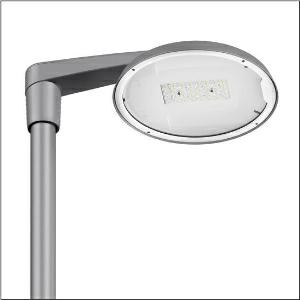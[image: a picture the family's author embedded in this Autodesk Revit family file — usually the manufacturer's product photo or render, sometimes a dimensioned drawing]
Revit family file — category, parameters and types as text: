
# Revit family: dl_r__50_iq_mini___st0_5a_5xa248b31f08fe_5b8c
name_source: partatom
category: Lighting Fixtures
units: mm (PartAtom-declared; Revit-internal decimal feet)

## family parameters
Cut with Voids When Loaded = No
Host = Face
Light Source = No
Part Type = Normal
Room Calculation Point = No
Round Connector Dimension = Use Diameter
Shared = No

## types (1)
- --- (1 x LED, 2700 lm, 16.3 W, 3000K)
    Apparent Load = 16 VA
    CIE Flux Codes = 41 75 97 100 100
    Color Rendering = 70
    Color Temperature = 3000K
    Default Elevation = 1800 mm
    Description = DL® 50 iQ mini, mast luminaire, primary light control with lens, of PMMA, primary optical cover: cover, of toughened safety glass, transparent, light distribution: ST0.5a, light emission: direct distribution, primary light characteristic: asymmetric, installation type: side-entry, post-top, LED, High Power LED, rated luminous flux: 2.700lm, luminous efficacy: 166lm/W, light colour: 730, colour temperature: 3000K, control: optimised constant luminous flux control (CLO 2.0), Desk-Remote (wireless, voltage-free reading and setting of iQ features in the workshop via application-optimized NFC function/RFID function), Light-Fading, Smart-Wire, Night-Set, Lumen-Switch, Temp-Guard, Auto-Match, Street-Remote, mains connection: 230..240V, AC, 50/60Hz, connection cable pre-assembled, cable length: 6,5m, start of lifetime: 16W, end of service life: 17W, reduction: 8W, luminaire housing, of diecast aluminium, powder-coated, Siteco® metallic grey (DB 702S), inclination adjustable: 0°, 5°, 10° (post-top) | 0°, -5°, -10°, -15° (side-entry), please order mast post-top element or mast side-entry element separately, diameter: 500mm, height: 115mm, post-top: for spigot size d x l = 76 x 100mm; with reducer (optional accessory) 60 x 100mm | side-entry: for spigot size d x l = 60 x 100mm; with reducer (optional accessory) 42 x 100mm, protection rating (complete): IP66, insulation class (complete): insulation class II (safety insulation), certification: CE, ENEC, VDE, impact resistance: IK08, permissible operating ambient temperature for outdoor applications: -25..+40°C, standard-compliant lighting for roads and squares, packaging unit: 1 piece

Light Distribution: ST0.5a
    Height = 115 mm
    Lamp = 1 x LED
    Lamp Light Flux = 2700 lm
    Lamp Power = 16.3 W
    Lamp count = 1
    Length = 500 mm
    Luminous efficacy = 166 lm/W
    Manufacturer = Siteco
    ModVariant = No
    Model = 5XA248B31F08FE
    Number of Poles = 1
    OnlyDefault = Yes
    Power Factor = 1
    Product Name = DL® 50 iQ mini | ST0.5a
    Product group = mast luminaire | pylon top
    ProductGroupID = 6100
    Protection Class = Protection class II
    Protection Degree = IP 66
    RLX_Detail_Level = 1
    RLX_Emergency_Light_Flux = 0 lm
    RLX_Emergency_Type = 0
    RLX_Emergency_Type_DB = No
    RlxData = <blob elided: 126445 chars, md5=ec054b3a>
    Socket = socket
    Standby Power = 0 W
    System Light Flux = 2700 lm
    System Power = 16 W
    Type Comments = factory setting: luminous flux: 100 % | dim-lin: 254 | 333 mA
    Type Image = l_1251794.jpg
    URL = http://relux.com
    VarID = @adj_088799
    Voltage = 0 V
    Weight = 0.00 kg
    Width = 0 mm  [stored 0 ft]

note: [stored X ft] marks values corroborated as IEEE doubles in the binary element streams (Revit-internal decimal feet)

## geometry (parser evidence)
native form markers: Blend x4, Sweep x13
no freeform markers — native parametric forms only
